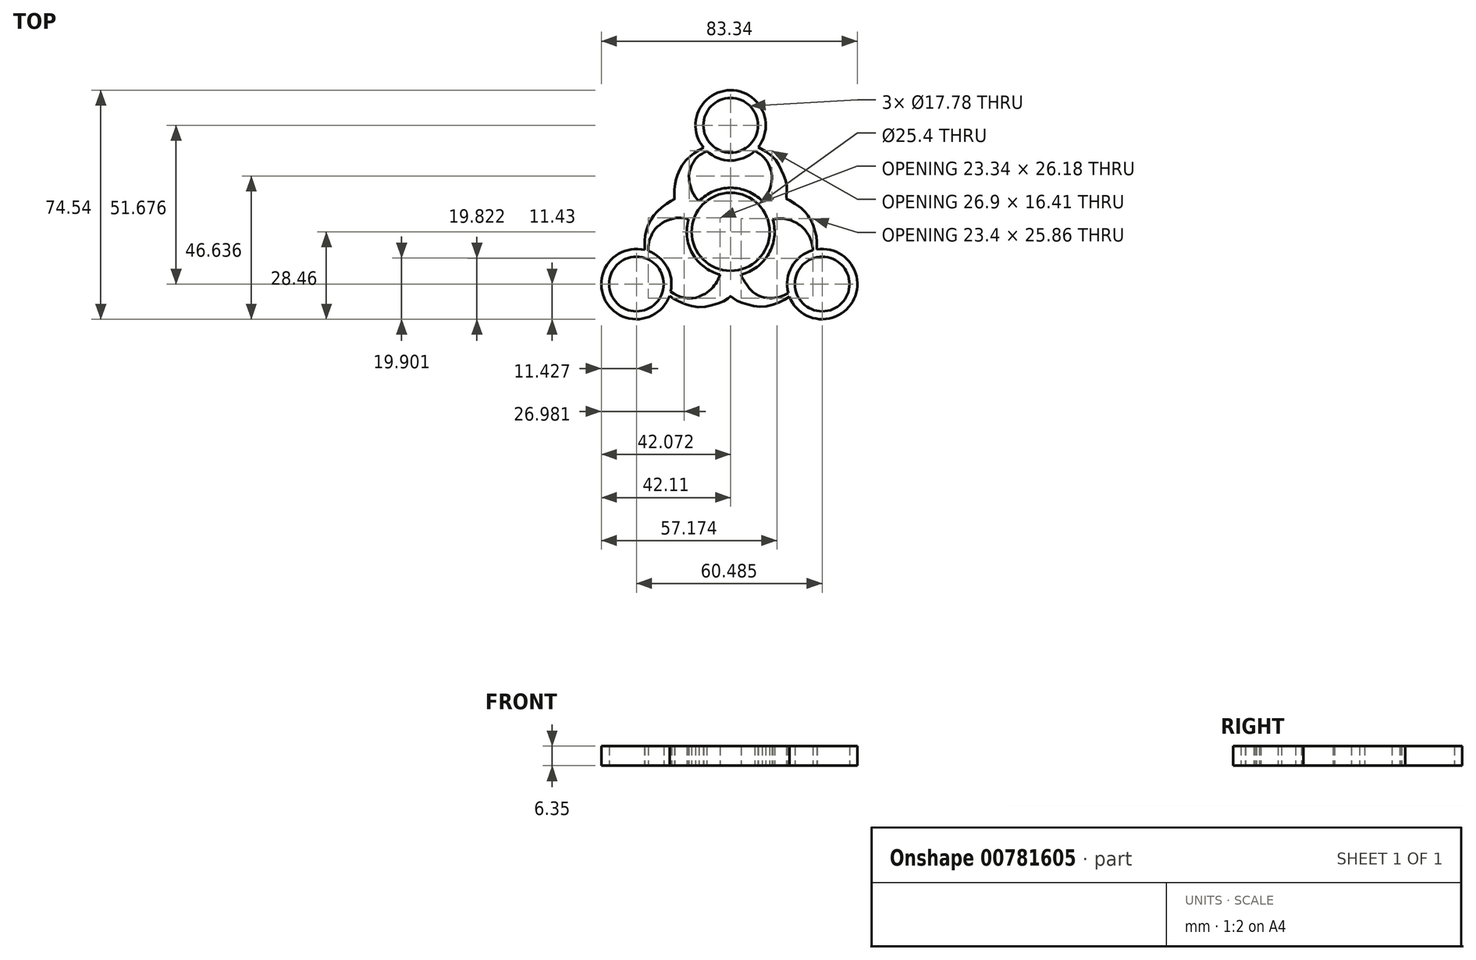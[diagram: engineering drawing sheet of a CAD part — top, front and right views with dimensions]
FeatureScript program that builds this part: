
annotation { "Feature Type Name" : "Feature", "Feature Type Description" : "" }
export const myFeature = defineFeature(function(context is Context, id is Id, definition is map)
    precondition{}
    {
        {
            var Q0;
            Q0=qCreatedBy(makeId("Top.planeOp"),FACE);
            var sketch = newSketch(context, id + "F0", { "sketchPlane" : qUnion([Q0])});
            skCircle(sketch, "E0", {"center": v(0, 0) * mm, "radius": 12.7 * mm});
            skFitSpline(sketch, "E1", {"points": [v(-9.03, 8.93) * mm, v(-11.65, 11.5) * mm, v(-13.04, 14.62) * mm, v(-13.48, 16.9) * mm, v(-13.43, 19.57) * mm, v(-12.54, 21.9) * mm, v(-11.15, 24.02) * mm, v(-9.76, 25.13) * mm, v(-7.48, 26.47) * mm, v(-6.24, 26.93) * mm, v(-4.88, 27.44) * mm, v(-4.75, 28.09) * mm, v(-4.74, 28.5) * mm, v(-5.67, 28.44) * mm, v(-7.02, 28.09) * mm, v(-8.6, 27.44) * mm, v(-10.22, 26.64) * mm, v(-11.23, 26.06) * mm, v(-12.46, 25.23) * mm, v(-13.58, 24.25) * mm, v(-14.8, 22.96) * mm, v(-15.73, 21.74) * mm, v(-16.36, 20.56) * mm, v(-17, 19.24) * mm, v(-17.62, 17.59) * mm, v(-17.78, 16.85) * mm, v(-17.97, 15.88) * mm, v(-18.22, 14.56) * mm, v(-18.33, 12.87) * mm, v(-18.26, 11.45) * mm, v(-18.2, 10.7) * mm, v(-18.87, 10.37) * mm, v(-19.61, 9.9) * mm, v(-20.66, 9.26) * mm, v(-22.11, 8.17) * mm, v(-23.67, 6.82) * mm, v(-24.61, 5.84) * mm, v(-25.42, 4.76) * mm, v(-26.2, 3.48) * mm, v(-26.88, 2.06) * mm, v(-27.25, 1.11) * mm, v(-27.76, -0.82) * mm, v(-27.96, -2.03) * mm, v(-28, -5.04) * mm, v(-27.73, -7.53) * mm, v(-27.68, -7.43) * mm, v(-27.53, -8.53) * mm, v(-27.06, -9.72) * mm, v(-26.96, -9.92) * mm, v(-26.44, -9.65) * mm, v(-26.54, -8.8) * mm, v(-26.77, -7.2) * mm, v(-26.8, -5.35) * mm, v(-26.6, -3.4) * mm, v(-25.86, -1.34) * mm, v(-24.26, 1.25) * mm, v(-21.08, 3.46) * mm, v(-17.9, 4.46) * mm, v(-15.31, 4.46) * mm, v(-13.04, 4.02) * mm, v(-12.17, 3.64) * mm], "startDerivative": vector(-112.63, 92.18) * mm, "endDerivative": vector(58.21, -30.64) * mm});
            skFitSpline(sketch, "E2", {"points": [v(-3.2, -12.29) * mm, v(-3.38, -13.6) * mm, v(-3.86, -15) * mm, v(-4.46, -16.3) * mm, v(-5.14, -17.25) * mm, v(-5.92, -18.24) * mm, v(-6.9, -19.12) * mm, v(-7.98, -19.98) * mm, v(-9.1, -20.56) * mm, v(-10.44, -21.17) * mm, v(-12, -21.53) * mm, v(-13.43, -21.64) * mm, v(-13.85, -21.65) * mm, v(-14.24, -21.65) * mm, v(-16.98, -20.92) * mm, v(-19.6, -19.4) * mm, v(-21.28, -18) * mm, v(-21.76, -17.84) * mm, v(-22.2, -18.22) * mm, v(-21.84, -18.73) * mm, v(-20.45, -20.25) * mm, v(-18.62, -21.76) * mm, v(-16.1, -23.03) * mm, v(-14.02, -23.72) * mm, v(-9.54, -24.58) * mm, v(-4.35, -23.31) * mm, v(-1.32, -22.1) * mm, v(0, -20.97) * mm, v(1.15, -21.92) * mm, v(3.74, -23.12) * mm, v(7.6, -24.2) * mm, v(11.77, -24.2) * mm, v(16.51, -22.68) * mm, v(19.86, -20.65) * mm, v(22.14, -18.5) * mm, v(21.8, -17.72) * mm, v(20.6, -18.77) * mm, v(18.87, -19.86) * mm, v(16.54, -20.99) * mm, v(14.36, -21.48) * mm, v(11.31, -21.48) * mm, v(7.97, -20.08) * mm, v(5.67, -17.87) * mm, v(4.13, -15.5) * mm, v(3.45, -14.14) * mm, v(3.12, -12.98) * mm, v(3.13, -12.3) * mm], "startDerivative": vector(-6.34, -73.95) * mm, "endDerivative": vector(5.17, 49.77) * mm});
            skArc(sketch, "E3", {"start": v(26.24, -9.66) * mm, "mid": v(23.42, 1.4) * mm, "end": v(12.2, 3.54) * mm});
            skFitSpline(sketch, "E4", {"points": [v(26.24, -9.66) * mm, v(27.1, -10.18) * mm, v(28.11, -4.7) * mm, v(27.62, -0.33) * mm, v(26.47, 3.03) * mm, v(25.41, 4.88) * mm, v(25.08, 5.37) * mm, v(22.98, 7.66) * mm, v(18.63, 10.46) * mm, v(18.2, 10.7) * mm, v(18.27, 12.4) * mm, v(18.07, 16.12) * mm, v(16.72, 19.64) * mm, v(14.82, 23.23) * mm, v(10.02, 26.95) * mm, v(4.27, 28.91) * mm, v(4.5, 27.63) * mm, v(6.26, 27.12) * mm, v(9.38, 25.4) * mm, v(11.3, 23.67) * mm, v(12.66, 21.3) * mm, v(13.33, 19.2) * mm, v(13.37, 16.56) * mm, v(12.62, 13.52) * mm, v(11.64, 11.76) * mm, v(10.6, 10.34) * mm, v(9.38, 9.22) * mm, v(9.04, 8.92) * mm], "startDerivative": vector(39.68, -43.11) * mm, "endDerivative": vector(-17.99, -16.52) * mm});
            skCircle(sketch, "E5", {"center": v(0, 0) * mm, "radius": 14.3 * mm});
            skCircle(sketch, "E6", {"center": v(0, 34.65) * mm, "radius": 8.9 * mm});
            skCircle(sketch, "E7", {"center": v(0, 34.65) * mm, "radius": 11.43 * mm});
            skCircle(sketch, "E8", {"center": v(29.8, -17.03) * mm, "radius": 8.9 * mm});
            skCircle(sketch, "E9", {"center": v(29.8, -17.03) * mm, "radius": 11.43 * mm});
            skCircle(sketch, "E10", {"center": v(-30.68, -17.03) * mm, "radius": 8.9 * mm});
            skCircle(sketch, "E11", {"center": v(-30.68, -17.03) * mm, "radius": 11.43 * mm});
            skSolve(sketch);
        }
        {
            var Q0;
            {var subQ0=sQuery(id+"F0.wireOp",EDGE,"E1");var subQ1=sQuery(id+"F0.wireOp",EDGE,"E0");var subQ2=makeQuery(id+"F0.imprint","INTERSECT",VERTEX,{"disambiguationData":[OD(0.0)],"derivedFrom":[subQ1,subQ0]});Q0=makeQuery(id+"F0.imprint","IMPRINT",FACE,{"disambiguationData":[TD([[makeQuery(id+"F0.imprint","IMPRINT",EDGE,{"disambiguationData":[TD([[subQ2,-1.0]])],"derivedFrom":subQ1}),-1.0]])]});}
            var Q1;
            {var subQ0=sQuery(id+"F0.wireOp",EDGE,"E5");var subQ1=sQuery(id+"F0.wireOp",EDGE,"E1");var subQ2=makeQuery(id+"F0.imprint","INTERSECT",VERTEX,{"disambiguationData":[OD(0.0)],"derivedFrom":[subQ1,subQ0]});Q1=makeQuery(id+"F0.imprint","IMPRINT",FACE,{"disambiguationData":[TD([[makeQuery(id+"F0.imprint","IMPRINT",EDGE,{"disambiguationData":[TD([[subQ2,-1.0]])],"derivedFrom":subQ1}),1.0]])]});}
            var Q2;
            {var subQ0=sQuery(id+"F0.wireOp",EDGE,"E1");var subQ1=sQuery(id+"F0.wireOp",EDGE,"E0");var subQ2=makeQuery(id+"F0.imprint","INTERSECT",VERTEX,{"disambiguationData":[OD(0.0)],"derivedFrom":[subQ1,subQ0]});Q2=makeQuery(id+"F0.imprint","IMPRINT",FACE,{"disambiguationData":[TD([[makeQuery(id+"F0.imprint","IMPRINT",EDGE,{"disambiguationData":[TD([[subQ2,1.0]])],"derivedFrom":subQ1}),-1.0]])]});}
            var Q3;
            {var subQ0=sQuery(id+"F0.wireOp",EDGE,"E3");var subQ1=sQuery(id+"F0.wireOp",EDGE,"E0");var subQ2=makeQuery(id+"F0.imprint","INTERSECT",VERTEX,{"derivedFrom":[subQ1,subQ0]});Q3=makeQuery(id+"F0.imprint","IMPRINT",FACE,{"disambiguationData":[TD([[makeQuery(id+"F0.imprint","IMPRINT",EDGE,{"disambiguationData":[TD([[subQ2,-1.0]])],"derivedFrom":subQ1}),-1.0]])]});}
            var Q4;
            {var subQ0=sQuery(id+"F0.wireOp",EDGE,"E2");var subQ1=sQuery(id+"F0.wireOp",EDGE,"E0");var subQ2=makeQuery(id+"F0.imprint","INTERSECT",VERTEX,{"disambiguationData":[OD(1.0)],"derivedFrom":[subQ1,subQ0]});Q4=makeQuery(id+"F0.imprint","IMPRINT",FACE,{"disambiguationData":[TD([[makeQuery(id+"F0.imprint","IMPRINT",EDGE,{"disambiguationData":[TD([[subQ2,-1.0]])],"derivedFrom":subQ1}),-1.0]])]});}
            var Q5;
            {var subQ0=sQuery(id+"F0.wireOp",EDGE,"E2");var subQ1=sQuery(id+"F0.wireOp",EDGE,"E0");var subQ2=makeQuery(id+"F0.imprint","INTERSECT",VERTEX,{"disambiguationData":[OD(0.0)],"derivedFrom":[subQ1,subQ0]});Q5=makeQuery(id+"F0.imprint","IMPRINT",FACE,{"disambiguationData":[TD([[makeQuery(id+"F0.imprint","IMPRINT",EDGE,{"disambiguationData":[TD([[subQ2,-1.0]])],"derivedFrom":subQ1}),-1.0]])]});}
            var Q6;
            {var subQ0=sQuery(id+"F0.wireOp",EDGE,"E1");var subQ1=sQuery(id+"F0.wireOp",EDGE,"E0");var subQ2=makeQuery(id+"F0.imprint","INTERSECT",VERTEX,{"disambiguationData":[OD(1.0)],"derivedFrom":[subQ1,subQ0]});Q6=makeQuery(id+"F0.imprint","IMPRINT",FACE,{"disambiguationData":[TD([[makeQuery(id+"F0.imprint","IMPRINT",EDGE,{"disambiguationData":[TD([[subQ2,-1.0]])],"derivedFrom":subQ1}),-1.0]])]});}
            var Q7;
            {var subQ0=sQuery(id+"F0.wireOp",EDGE,"E5");var subQ1=sQuery(id+"F0.wireOp",EDGE,"E2");var subQ2=makeQuery(id+"F0.imprint","INTERSECT",VERTEX,{"disambiguationData":[OD(0.0)],"derivedFrom":[subQ1,subQ0]});Q7=makeQuery(id+"F0.imprint","IMPRINT",FACE,{"disambiguationData":[TD([[makeQuery(id+"F0.imprint","IMPRINT",EDGE,{"disambiguationData":[TD([[subQ2,-1.0]])],"derivedFrom":subQ1}),1.0]])]});}
            var Q8;
            {var subQ5=sQuery(id+"F0.wireOp",EDGE,"E9");var subQ8=sQuery(id+"F0.wireOp",EDGE,"E3");var subQ10=makeQuery(id+"F0.imprint","INTERSECT",VERTEX,{"derivedFrom":[subQ8,subQ5]});Q8=makeQuery(id+"F0.imprint","IMPRINT",FACE,{"disambiguationData":[TD([[makeQuery(id+"F0.imprint","IMPRINT",EDGE,{"disambiguationData":[TD([[subQ10,-1.0]])],"derivedFrom":subQ8}),-1.0]])]});}
            var Q9;
            {var subQ0=sQuery(id+"F0.wireOp",EDGE,"E7");var subQ1=sQuery(id+"F0.wireOp",EDGE,"E1");var subQ2=makeQuery(id+"F0.imprint","INTERSECT",VERTEX,{"disambiguationData":[OD(0.0)],"derivedFrom":[subQ1,subQ0]});Q9=makeQuery(id+"F0.imprint","IMPRINT",FACE,{"disambiguationData":[TD([[makeQuery(id+"F0.imprint","IMPRINT",EDGE,{"disambiguationData":[TD([[subQ2,1.0]])],"derivedFrom":subQ1}),-1.0]])]});}
            var Q10;
            {var subQ0=sQuery(id+"F0.wireOp",EDGE,"E7");var subQ1=sQuery(id+"F0.wireOp",EDGE,"E1");var subQ2=makeQuery(id+"F0.imprint","INTERSECT",VERTEX,{"disambiguationData":[OD(1.0)],"derivedFrom":[subQ1,subQ0]});Q10=makeQuery(id+"F0.imprint","IMPRINT",FACE,{"disambiguationData":[TD([[makeQuery(id+"F0.imprint","IMPRINT",EDGE,{"disambiguationData":[TD([[subQ2,-1.0]])],"derivedFrom":subQ1}),-1.0]])]});}
            var Q11;
            {var subQ0=sQuery(id+"F0.wireOp",EDGE,"E7");var subQ1=sQuery(id+"F0.wireOp",EDGE,"E1");var subQ2=makeQuery(id+"F0.imprint","INTERSECT",VERTEX,{"disambiguationData":[OD(1.0)],"derivedFrom":[subQ1,subQ0]});Q11=makeQuery(id+"F0.imprint","IMPRINT",FACE,{"disambiguationData":[TD([[makeQuery(id+"F0.imprint","IMPRINT",EDGE,{"disambiguationData":[TD([[subQ2,-1.0]])],"derivedFrom":subQ1}),1.0]])]});}
            var Q12;
            {var subQ0=sQuery(id+"F0.wireOp",EDGE,"E8");var subQ1=sQuery(id+"F0.wireOp",EDGE,"E2");var subQ2=makeQuery(id+"F0.imprint","INTERSECT",VERTEX,{"disambiguationData":[OD(1.0)],"derivedFrom":[subQ1,subQ0]});Q12=makeQuery(id+"F0.imprint","IMPRINT",FACE,{"disambiguationData":[TD([[makeQuery(id+"F0.imprint","IMPRINT",EDGE,{"disambiguationData":[TD([[subQ2,-1.0]])],"derivedFrom":subQ1}),-1.0]])]});}
            var Q13;
            {var subQ0=sQuery(id+"F0.wireOp",EDGE,"E9");var subQ1=sQuery(id+"F0.wireOp",EDGE,"E2");var subQ2=makeQuery(id+"F0.imprint","INTERSECT",VERTEX,{"disambiguationData":[OD(0.0)],"derivedFrom":[subQ1,subQ0]});Q13=makeQuery(id+"F0.imprint","IMPRINT",FACE,{"disambiguationData":[TD([[makeQuery(id+"F0.imprint","IMPRINT",EDGE,{"disambiguationData":[TD([[subQ2,-1.0]])],"derivedFrom":subQ1}),-1.0]])]});}
            var Q14;
            {var subQ0=sQuery(id+"F0.wireOp",EDGE,"E8");var subQ1=sQuery(id+"F0.wireOp",EDGE,"E3");var subQ2=makeQuery(id+"F0.imprint","INTERSECT",VERTEX,{"derivedFrom":[subQ1,subQ0]});Q14=makeQuery(id+"F0.imprint","IMPRINT",FACE,{"disambiguationData":[TD([[makeQuery(id+"F0.imprint","IMPRINT",EDGE,{"disambiguationData":[TD([[subQ2,-1.0]])],"derivedFrom":subQ1}),-1.0]])]});}
            var Q15;
            {var subQ0=sQuery(id+"F0.wireOp",EDGE,"E9");var subQ1=sQuery(id+"F0.wireOp",EDGE,"E2");var subQ2=makeQuery(id+"F0.imprint","INTERSECT",VERTEX,{"disambiguationData":[OD(0.0)],"derivedFrom":[subQ1,subQ0]});Q15=makeQuery(id+"F0.imprint","IMPRINT",FACE,{"disambiguationData":[TD([[makeQuery(id+"F0.imprint","IMPRINT",EDGE,{"disambiguationData":[TD([[subQ2,-1.0]])],"derivedFrom":subQ1}),1.0]])]});}
            var Q16;
            {var subQ0=sQuery(id+"F0.wireOp",EDGE,"E11");var subQ1=sQuery(id+"F0.wireOp",EDGE,"E2");var subQ2=makeQuery(id+"F0.imprint","INTERSECT",VERTEX,{"disambiguationData":[OD(1.0)],"derivedFrom":[subQ1,subQ0]});Q16=makeQuery(id+"F0.imprint","IMPRINT",FACE,{"disambiguationData":[TD([[makeQuery(id+"F0.imprint","IMPRINT",EDGE,{"disambiguationData":[TD([[subQ2,-1.0]])],"derivedFrom":subQ1}),1.0]])]});}
            var Q17;
            {var subQ0=sQuery(id+"F0.wireOp",EDGE,"E10");var subQ1=sQuery(id+"F0.wireOp",EDGE,"E1");var subQ2=makeQuery(id+"F0.imprint","INTERSECT",VERTEX,{"disambiguationData":[OD(1.0)],"derivedFrom":[subQ1,subQ0]});Q17=makeQuery(id+"F0.imprint","IMPRINT",FACE,{"disambiguationData":[TD([[makeQuery(id+"F0.imprint","IMPRINT",EDGE,{"disambiguationData":[TD([[subQ2,-1.0]])],"derivedFrom":subQ1}),-1.0]])]});}
            var Q18;
            {var subQ0=sQuery(id+"F0.wireOp",EDGE,"E11");var subQ1=sQuery(id+"F0.wireOp",EDGE,"E1");var subQ2=makeQuery(id+"F0.imprint","INTERSECT",VERTEX,{"disambiguationData":[OD(0.0)],"derivedFrom":[subQ1,subQ0]});Q18=makeQuery(id+"F0.imprint","IMPRINT",FACE,{"disambiguationData":[TD([[makeQuery(id+"F0.imprint","IMPRINT",EDGE,{"disambiguationData":[TD([[subQ2,-1.0]])],"derivedFrom":subQ1}),-1.0]])]});}
            var Q19;
            {var subQ0=sQuery(id+"F0.wireOp",EDGE,"E11");var subQ1=sQuery(id+"F0.wireOp",EDGE,"E1");var subQ2=makeQuery(id+"F0.imprint","INTERSECT",VERTEX,{"disambiguationData":[OD(0.0)],"derivedFrom":[subQ1,subQ0]});Q19=makeQuery(id+"F0.imprint","IMPRINT",FACE,{"disambiguationData":[TD([[makeQuery(id+"F0.imprint","IMPRINT",EDGE,{"disambiguationData":[TD([[subQ2,-1.0]])],"derivedFrom":subQ1}),1.0]])]});}
            var Q20;
            {var subQ0=sQuery(id+"F0.wireOp",EDGE,"E7");var subQ1=sQuery(id+"F0.wireOp",EDGE,"E4");var subQ2=makeQuery(id+"F0.imprint","INTERSECT",VERTEX,{"disambiguationData":[OD(0.0)],"derivedFrom":[subQ1,subQ0]});Q20=makeQuery(id+"F0.imprint","IMPRINT",FACE,{"disambiguationData":[TD([[makeQuery(id+"F0.imprint","IMPRINT",EDGE,{"disambiguationData":[TD([[subQ2,-1.0]])],"derivedFrom":subQ1}),1.0]])]});}
            extrude(context, id + "F1", {"entities" : qUnion([Q0, Q1, Q2, Q3, Q4, Q5, Q6, Q7, Q8, Q9, Q10, Q11, Q12, Q13, Q14, Q15, Q16, Q17, Q18, Q19, Q20]), "depth" : 6.35 * mm, "offsetDistance" : 25 * mm});
        }
    });
